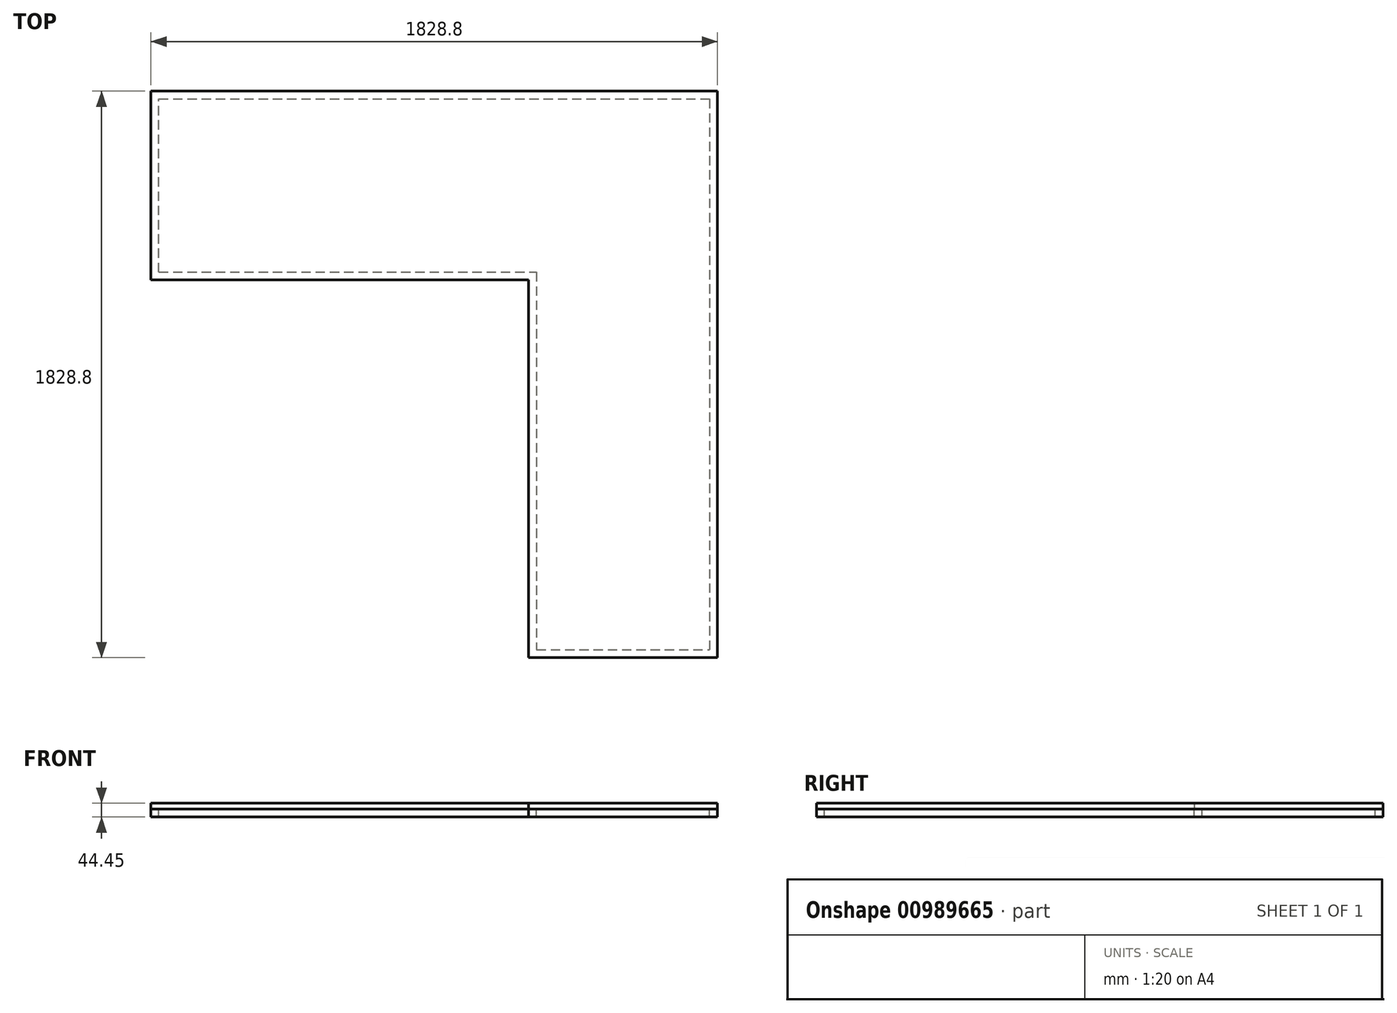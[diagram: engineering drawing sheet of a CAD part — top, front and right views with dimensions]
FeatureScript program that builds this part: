
annotation { "Feature Type Name" : "Feature", "Feature Type Description" : "" }
export const myFeature = defineFeature(function(context is Context, id is Id, definition is map)
    precondition{}
    {
        {
            var Q0;
            Q0=qCreatedBy(makeId("Top.planeOp"),FACE);
            var sketch = newSketch(context, id + "F0", { "sketchPlane" : qUnion([Q0])});
            skLineSegment(sketch, "E0.bottom", {"start": v(0, 0) * mm, "end": v(1219.2, 0) * mm});
            skLineSegment(sketch, "E0.top", {"start": v(0, 609.6) * mm, "end": v(1828.8, 609.6) * mm});
            skLineSegment(sketch, "E0.left", {"start": v(0, 0) * mm, "end": v(0, 609.6) * mm});
            skLineSegment(sketch, "E0.right", {"start": v(1828.8, 0) * mm, "end": v(1828.8, 609.6) * mm});
            skLineSegment(sketch, "E1.top", {"start": v(1828.8, -1219.2) * mm, "end": v(1219.2, -1219.2) * mm});
            skLineSegment(sketch, "E1.left", {"start": v(1828.8, 0) * mm, "end": v(1828.8, -1219.2) * mm});
            skLineSegment(sketch, "E1.right", {"start": v(1219.2, 0) * mm, "end": v(1219.2, -1219.2) * mm});
            skSolve(sketch);
        }
        {
            var Q0;
            Q0=makeQuery(id+"F0.imprint","IMPRINT",FACE,{"disambiguationData":[TD([[makeQuery(id+"F0.imprint","IMPRINT",EDGE,{"derivedFrom":sQuery(id+"F0.wireOp",EDGE,"E0.bottom")}),1.0]])]});
            extrude(context, id + "F1", {"entities" : qUnion([Q0]), "depth" : 19.05 * mm, "offsetDistance" : 25.4 * mm});
        }
        {
            var Q0;
            Q0=makeQuery(id+"F1.opExtrude","CAP_FACE",FACE,{"disambiguationData":[OSD([sQuery(id+"F0.wireOp",EDGE,"E0.bottom"),sQuery(id+"F0.wireOp",EDGE,"E0.top"),sQuery(id+"F0.wireOp",EDGE,"E0.left"),sQuery(id+"F0.wireOp",EDGE,"E0.right"),sQuery(id+"F0.wireOp",EDGE,"E1.top"),sQuery(id+"F0.wireOp",EDGE,"E1.left"),sQuery(id+"F0.wireOp",EDGE,"E1.right")])],"isStart":true});
            var sketch = newSketch(context, id + "F2", { "sketchPlane" : qUnion([Q0])});
            skLineSegment(sketch, "E2.top", {"start": v(1218.58, 0) * mm, "end": v(1219.85, 0) * mm});
            skLineSegment(sketch, "E3", {"start": v(25.4, -25.4) * mm, "end": v(1244.6, -25.4) * mm});
            skLineSegment(sketch, "E4", {"start": v(1244.6, -25.4) * mm, "end": v(1244.6, 1193.8) * mm});
            skLineSegment(sketch, "E5", {"start": v(25.4, -584.2) * mm, "end": v(1803.4, -584.2) * mm});
            skLineSegment(sketch, "E6", {"start": v(1803.4, -584.2) * mm, "end": v(1803.4, 1193.8) * mm});
            skLineSegment(sketch, "E7", {"start": v(25.4, -25.4) * mm, "end": v(25.4, -584.2) * mm});
            skLineSegment(sketch, "E8", {"start": v(1244.6, 1193.8) * mm, "end": v(1803.4, 1193.8) * mm});
            skSolve(sketch);
        }
        {
            var Q0;
            Q0=makeQuery(id+"F2.imprint","IMPRINT",FACE,{"disambiguationData":[TD([[makeQuery(id+"F2.imprint","IMPRINT",EDGE,{"derivedFrom":sQuery(id+"F2.wireOp",EDGE,"E3")}),1.0]])]});
            extrude(context, id + "F3", {"entities" : qUnion([Q0]), "depth" : 25.4 * mm, "offsetDistance" : 25.4 * mm});
        }
    });
